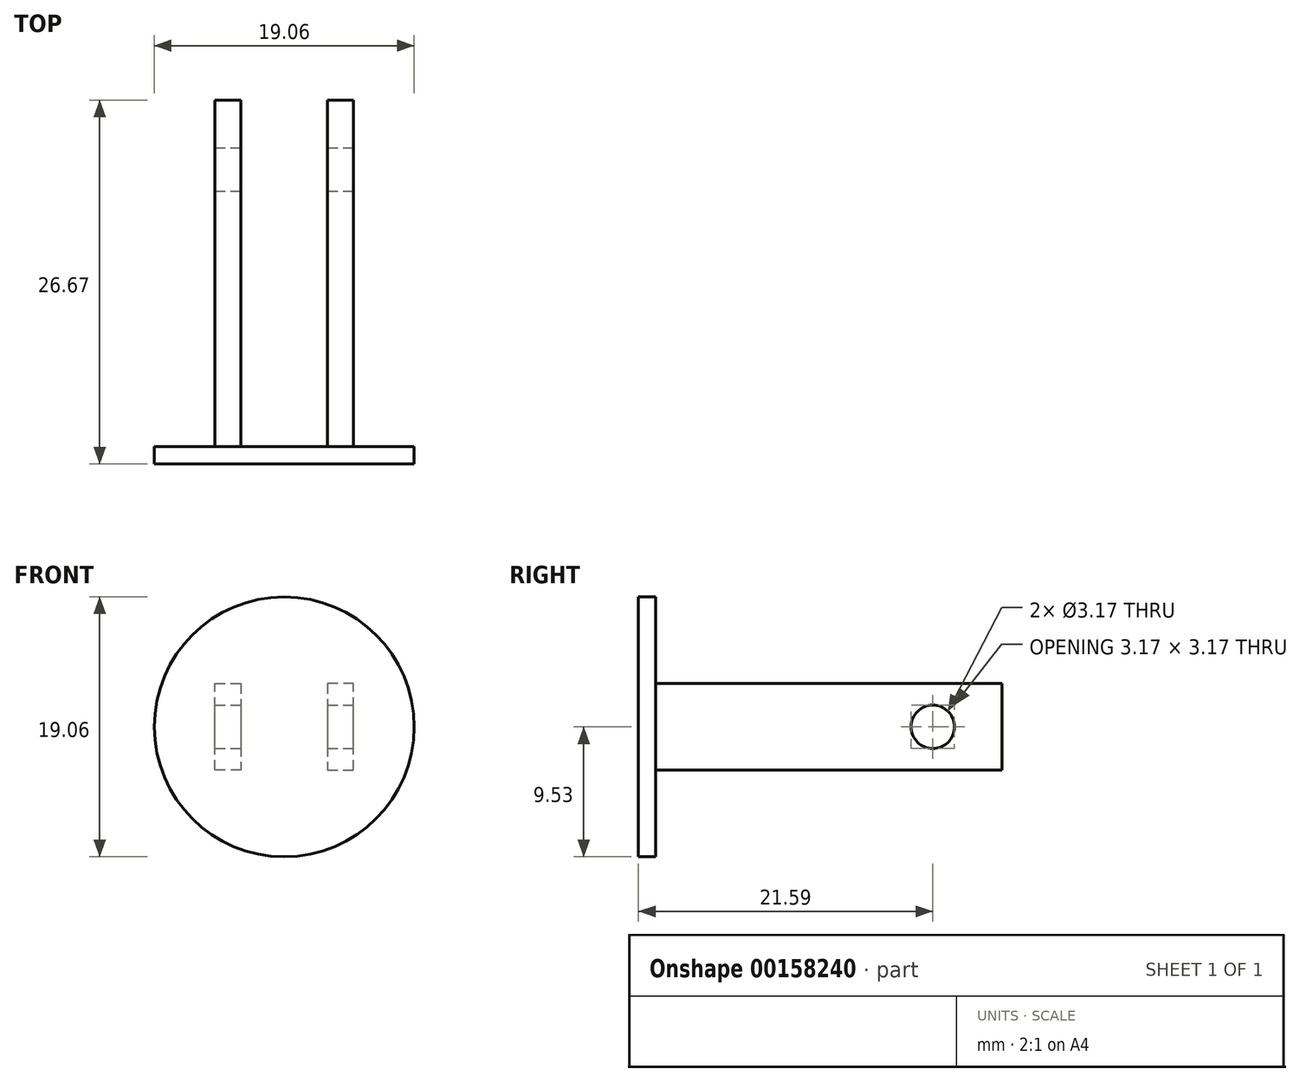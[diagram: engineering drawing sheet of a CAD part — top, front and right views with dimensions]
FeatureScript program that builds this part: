
annotation { "Feature Type Name" : "Feature", "Feature Type Description" : "" }
export const myFeature = defineFeature(function(context is Context, id is Id, definition is map)
    precondition{}
    {
        {
            var Q0;
            Q0=qCreatedBy(makeId("Front.planeOp"),FACE);
            var sketch = newSketch(context, id + "F0", { "sketchPlane" : qUnion([Q0])});
            skCircle(sketch, "E0", {"center": v(0, 0) * mm, "radius": 9.53 * mm});
            skSolve(sketch);
        }
        {
            var Q0;
            Q0 = qSketchRegion(id + "F0", true);
            extrude(context, id + "F1", {"entities" : qUnion([Q0]), "depth" : 1.27 * mm});
        }
        {
            var Q0;
            Q0=makeQuery(id+"F1.opExtrude","CAP_FACE",FACE,{"disambiguationData":[OSD([sQuery(id+"F0.wireOp",EDGE,"E0")])],"isStart":true});
            var sketch = newSketch(context, id + "F2", { "sketchPlane" : qUnion([Q0])});
            skLineSegment(sketch, "E1", {"start": v(0, 13.48) * mm, "end": v(0, -15.75) * mm});
            skLineSegment(sketch, "E2", {"start": v(-3.17, 3.18) * mm, "end": v(-3.17, -3.18) * mm});
            skLineSegment(sketch, "E3", {"start": v(-3.17, -3.17) * mm, "end": v(-5.08, -3.17) * mm});
            skLineSegment(sketch, "E4", {"start": v(-5.08, -3.18) * mm, "end": v(-5.08, 3.18) * mm});
            skLineSegment(sketch, "E5", {"start": v(-5.08, 3.18) * mm, "end": v(-3.17, 3.18) * mm});
            skLineSegment(sketch, "E6.MirrorCS", {"start": v(3.17, 3.18) * mm, "end": v(3.17, -3.18) * mm});
            skLineSegment(sketch, "E7.MirrorCS", {"start": v(3.17, -3.17) * mm, "end": v(5.08, -3.17) * mm});
            skLineSegment(sketch, "E8.MirrorCS", {"start": v(5.08, -3.18) * mm, "end": v(5.08, 3.18) * mm});
            skLineSegment(sketch, "E9.MirrorCS", {"start": v(5.08, 3.18) * mm, "end": v(3.17, 3.18) * mm});
            skSolve(sketch);
        }
        {
            var Q0;
            Q0 = qSketchRegion(id + "F2", true);
            extrude(context, id + "F3", {"entities" : qUnion([Q0]), "operationType" : NewBodyOperationType.ADD, "depth" : 25.4 * mm});
        }
        {
            var Q0;
            Q0=makeQuery(id+"F3.opExtrude","SWEPT_FACE",FACE,{"disambiguationData":[OSD([sQuery(id+"F2.wireOp",EDGE,"E4")])]});
            var sketch = newSketch(context, id + "F4", { "sketchPlane" : qUnion([Q0])});
            skCircle(sketch, "E10", {"center": v(20.32, 0) * mm, "radius": 1.59 * mm});
            skSolve(sketch);
        }
        {
            var Q0;
            Q0 = qSketchRegion(id + "F4", true);
            extrude(context, id + "F5", {"entities" : qUnion([Q0]), "operationType" : NewBodyOperationType.REMOVE, "endBound" : BoundingType.THROUGH_ALL, "oppositeDirection" : true, "depth" : 25.4 * mm});
        }
    });
